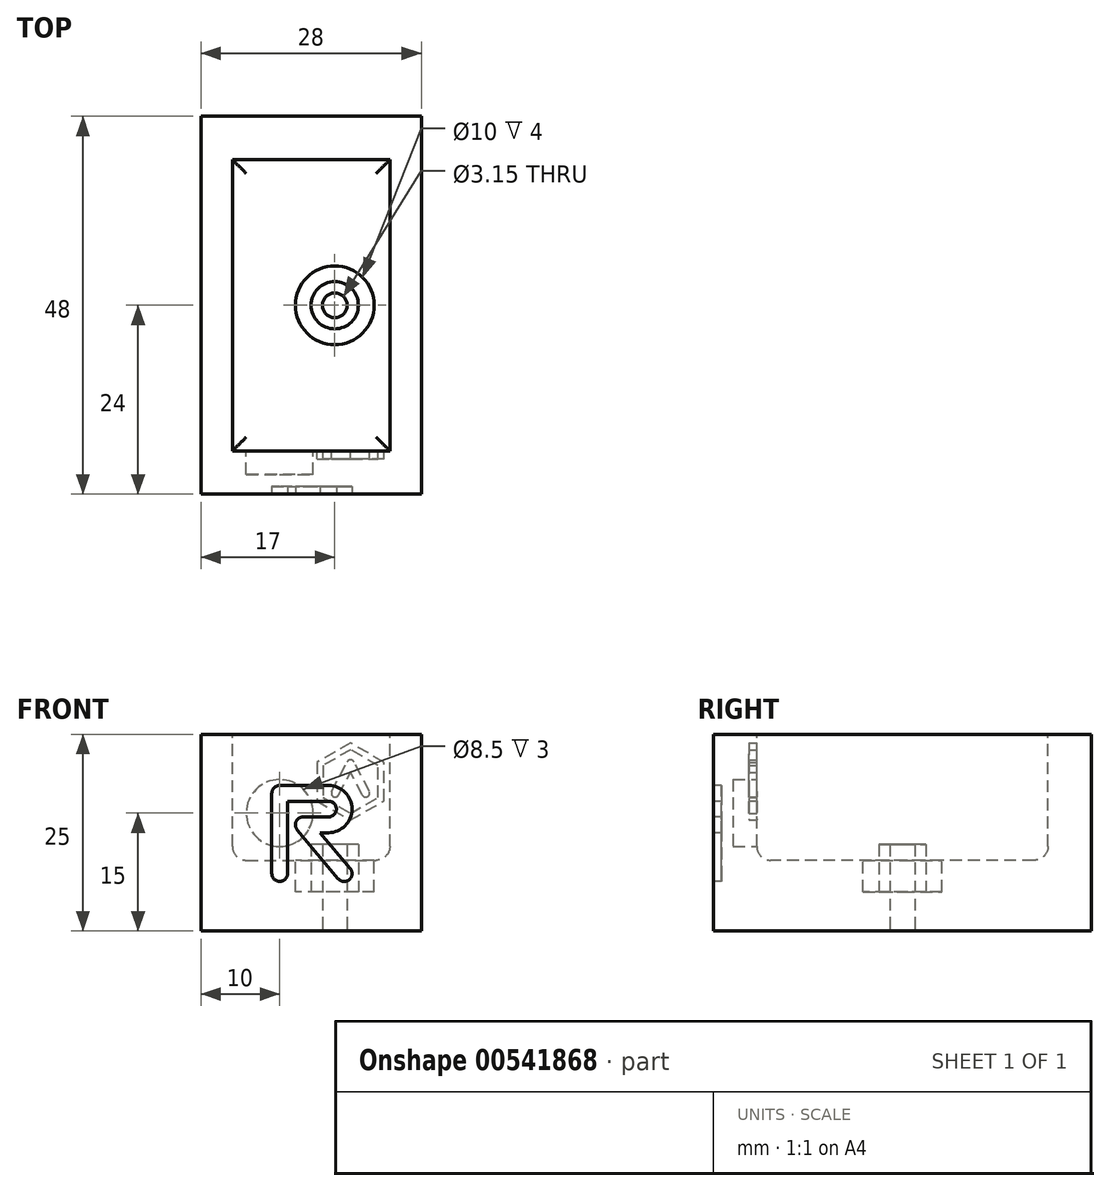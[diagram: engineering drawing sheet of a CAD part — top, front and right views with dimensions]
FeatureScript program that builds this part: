
annotation { "Feature Type Name" : "Feature", "Feature Type Description" : "" }
export const myFeature = defineFeature(function(context is Context, id is Id, definition is map)
    precondition{}
    {
        {
            var Q0;
            Q0=qCreatedBy(makeId("Top.planeOp"),FACE);
            var sketch = newSketch(context, id + "F0", { "sketchPlane" : qUnion([Q0])});
            skLineSegment(sketch, "E0.bottom", {"start": v(-28, 48) * mm, "end": v(0, 48) * mm});
            skLineSegment(sketch, "E0.top", {"start": v(-28, 0) * mm, "end": v(0, 0) * mm});
            skLineSegment(sketch, "E0.left", {"start": v(-28, 48) * mm, "end": v(-28, 0) * mm});
            skLineSegment(sketch, "E0.right", {"start": v(0, 48) * mm, "end": v(0, 0) * mm});
            skSolve(sketch);
        }
        {
            var Q0;
            Q0=makeQuery(id+"F0.imprint","IMPRINT",FACE,{"disambiguationData":[TD([[makeQuery(id+"F0.imprint","IMPRINT",EDGE,{"derivedFrom":sQuery(id+"F0.wireOp",EDGE,"E0.bottom")}),-1.0]])]});
            extrude(context, id + "F1", {"entities" : qUnion([Q0]), "depth" : 25 * mm, "offsetDistance" : 25 * mm});
        }
        {
            var Q0;
            Q0=makeQuery(id+"F1.opExtrude","CAP_FACE",FACE,{"disambiguationData":[OSD([sQuery(id+"F0.wireOp",EDGE,"E0.bottom"),sQuery(id+"F0.wireOp",EDGE,"E0.top"),sQuery(id+"F0.wireOp",EDGE,"E0.left"),sQuery(id+"F0.wireOp",EDGE,"E0.right")])],"isStart":false});
            var sketch = newSketch(context, id + "F2", { "sketchPlane" : qUnion([Q0])});
            skLineSegment(sketch, "E1.bottom", {"start": v(-24, 42.5) * mm, "end": v(-4, 42.5) * mm});
            skLineSegment(sketch, "E1.top", {"start": v(-24, 5.5) * mm, "end": v(-4, 5.5) * mm});
            skLineSegment(sketch, "E1.left", {"start": v(-24, 42.5) * mm, "end": v(-24, 5.5) * mm});
            skLineSegment(sketch, "E1.right", {"start": v(-4, 42.5) * mm, "end": v(-4, 5.5) * mm});
            skSolve(sketch);
        }
        {
            var Q0;
            Q0=qSketchRegion(id+"F2",true);
            extrude(context, id + "F3", {"entities" : qUnion([Q0]), "operationType" : NewBodyOperationType.REMOVE, "oppositeDirection" : true, "depth" : 16 * mm, "offsetDistance" : 25 * mm});
        }
        {
            var Q0;
            Q0=makeQuery(id+"F3.boolean.opBoolean","COPY",FACE,{"derivedFrom":makeQuery(id+"F3.opExtrude","CAP_FACE",FACE,{"disambiguationData":[OSD([sQuery(id+"F2.wireOp",EDGE,"E1.bottom"),sQuery(id+"F2.wireOp",EDGE,"E1.top"),sQuery(id+"F2.wireOp",EDGE,"E1.left"),sQuery(id+"F2.wireOp",EDGE,"E1.right")])],"isStart":false})});
            var sketch = newSketch(context, id + "F4", { "sketchPlane" : qUnion([Q0])});
            skCircle(sketch, "E2", {"center": v(-11, 24) * mm, "radius": 3 * mm});
            skCircle(sketch, "E3", {"center": v(-11, 24) * mm, "radius": 1.57 * mm});
            skSolve(sketch);
        }
        {
            var Q0;
            Q0=qSketchRegion(id+"F4",true);
            extrude(context, id + "F5", {"entities" : qUnion([Q0]), "operationType" : NewBodyOperationType.ADD, "depth" : 2 * mm, "offsetDistance" : 25 * mm});
        }
        {
            var Q0;
            {var subQ0=sQuery(id+"F2.wireOp",EDGE,"E1.right");var subQ1=sQuery(id+"F2.wireOp",EDGE,"E1.left");var subQ2=sQuery(id+"F2.wireOp",EDGE,"E1.top");var subQ3=sQuery(id+"F2.wireOp",EDGE,"E1.bottom");Q0=makeQuery(id+"F5.boolean.opBoolean","SPLIT",FACE,{"disambiguationData":[TD([makeQuery(id+"F3.boolean.opBoolean","COPY",FACE,{"derivedFrom":makeQuery(id+"F3.opExtrude","SWEPT_FACE",FACE,{"disambiguationData":[OSD([subQ3])]})})])],"derivedFrom":makeQuery(id+"F3.boolean.opBoolean","COPY",FACE,{"derivedFrom":makeQuery(id+"F3.opExtrude","CAP_FACE",FACE,{"disambiguationData":[OSD([subQ3,subQ2,subQ1,subQ0])],"isStart":false})})});}
            var sketch = newSketch(context, id + "F6", { "sketchPlane" : qUnion([Q0])});
            skCircle(sketch, "E4", {"center": v(-11, 24) * mm, "radius": 5 * mm});
            skCircle(sketch, "E5", {"center": v(-11, 24) * mm, "radius": 3 * mm});
            skSolve(sketch);
        }
        {
            var Q0;
            Q0=qSketchRegion(id+"F6",true);
            extrude(context, id + "F7", {"entities" : qUnion([Q0]), "operationType" : NewBodyOperationType.REMOVE, "oppositeDirection" : true, "depth" : 4 * mm, "offsetDistance" : 25 * mm});
        }
        {
            var Q0;
            Q0=makeQuery(id+"F3.boolean.opBoolean","COPY",FACE,{"derivedFrom":makeQuery(id+"F3.opExtrude","SWEPT_FACE",FACE,{"disambiguationData":[OSD([sQuery(id+"F2.wireOp",EDGE,"E1.top")])]})});
            var sketch = newSketch(context, id + "F8", { "sketchPlane" : qUnion([Q0])});
            skCircle(sketch, "E6", {"center": v(18, 15) * mm, "radius": 4.25 * mm});
            skSolve(sketch);
        }
        {
            var Q0;
            Q0=makeQuery(id+"F8.imprint","IMPRINT",FACE,{"disambiguationData":[TD([[makeQuery(id+"F8.imprint","IMPRINT",EDGE,{"derivedFrom":sQuery(id+"F8.wireOp",EDGE,"E6")}),1.0]])]});
            var Q1;
            Q1=sQuery(id+"F8.wireOp",EDGE,"E6");
            extrude(context, id + "F9", {"entities" : qUnion([Q0]), "operationType" : NewBodyOperationType.REMOVE, "surfaceEntities" : qUnion([Q1]), "oppositeDirection" : true, "depth" : 3 * mm, "offsetDistance" : 25 * mm});
        }
        {
            var Q0;
            Q0=makeQuery(id+"F5.boolean.opBoolean","SPLIT",FACE,{"disambiguationData":[TD([makeQuery(id+"F5.opExtrude","SWEPT_FACE",FACE,{"disambiguationData":[OSD([sQuery(id+"F4.wireOp",EDGE,"E3")])]})])],"derivedFrom":makeQuery(id+"F3.boolean.opBoolean","COPY",FACE,{"derivedFrom":makeQuery(id+"F3.opExtrude","CAP_FACE",FACE,{"disambiguationData":[OSD([sQuery(id+"F2.wireOp",EDGE,"E1.bottom"),sQuery(id+"F2.wireOp",EDGE,"E1.top"),sQuery(id+"F2.wireOp",EDGE,"E1.left"),sQuery(id+"F2.wireOp",EDGE,"E1.right")])],"isStart":false})})});
            extrude(context, id + "F10", {"entities" : qUnion([Q0]), "operationType" : NewBodyOperationType.REMOVE, "endBound" : BoundingType.THROUGH_ALL, "oppositeDirection" : true, "depth" : 25 * mm, "offsetDistance" : 25 * mm});
        }
        {
            var Q0;
            Q0=makeQuery(id+"F3.boolean.opBoolean","COPY",FACE,{"derivedFrom":makeQuery(id+"F3.opExtrude","SWEPT_FACE",FACE,{"disambiguationData":[OSD([sQuery(id+"F2.wireOp",EDGE,"E1.bottom")])]})});
            var sketch = newSketch(context, id + "F11", { "sketchPlane" : qUnion([Q0])});
            skCircle(sketch, "E7", {"center": v(-18, 15) * mm, "radius": 4.25 * mm});
            skSolve(sketch);
        }
        {
            var Q0;
            Q0=makeQuery(id+"F1.opExtrude","SWEPT_FACE",FACE,{"disambiguationData":[OSD([sQuery(id+"F0.wireOp",EDGE,"E0.bottom")])]});
            var sketch = newSketch(context, id + "F12", { "sketchPlane" : qUnion([Q0])});
            skLineSegment(sketch, "E8", {"start": v(10, 19) * mm, "end": v(10, 7) * mm});
            skLineSegment(sketch, "E9", {"start": v(11, 6) * mm, "end": v(17, 6) * mm});
            skLineSegment(sketch, "E10", {"start": v(18, 7) * mm, "end": v(18, 7) * mm});
            skLineSegment(sketch, "E11", {"start": v(17, 8) * mm, "end": v(12.5, 8) * mm});
            skLineSegment(sketch, "E12", {"start": v(12, 8.5) * mm, "end": v(12, 19) * mm});
            skLineSegment(sketch, "E13", {"start": v(11, 20) * mm, "end": v(11, 20) * mm});
            skPoint(sketch, "E14.visualSharp", {"position": v(10, 20) * mm});
            skArc(sketch, "E14.filletArc", {"start": v(11, 20) * mm, "mid": v(10.3, 19.7) * mm, "end": v(10, 19) * mm});
            skPoint(sketch, "E15.visualSharp", {"position": v(12, 20) * mm});
            skArc(sketch, "E15.filletArc", {"start": v(12, 19) * mm, "mid": v(11.7, 19.7) * mm, "end": v(11, 20) * mm});
            skPoint(sketch, "E16.visualSharp", {"position": v(10, 6) * mm});
            skArc(sketch, "E16.filletArc", {"start": v(10, 7) * mm, "mid": v(10.3, 6.3) * mm, "end": v(11, 6) * mm});
            skPoint(sketch, "E17.visualSharp", {"position": v(12, 8) * mm});
            skArc(sketch, "E17.filletArc", {"start": v(12, 8.5) * mm, "mid": v(12.15, 8.15) * mm, "end": v(12.5, 8) * mm});
            skPoint(sketch, "E18.visualSharp", {"position": v(18, 8) * mm});
            skArc(sketch, "E18.filletArc", {"start": v(18, 7) * mm, "mid": v(17.7, 7.7) * mm, "end": v(17, 8) * mm});
            skPoint(sketch, "E19.visualSharp", {"position": v(18, 6) * mm});
            skArc(sketch, "E19.filletArc", {"start": v(17, 6) * mm, "mid": v(17.7, 6.3) * mm, "end": v(18, 7) * mm});
            skSolve(sketch);
        }
        {
            var Q0;
            Q0=makeQuery(id+"F1.opExtrude","SWEPT_FACE",FACE,{"disambiguationData":[OSD([sQuery(id+"F0.wireOp",EDGE,"E0.top")])]});
            var sketch = newSketch(context, id + "F13", { "sketchPlane" : qUnion([Q0])});
            skLineSegment(sketch, "E20", {"start": v(-17, 7.3) * mm, "end": v(-17, 18.5) * mm});
            skLineSegment(sketch, "E21", {"start": v(-17, 18.5) * mm, "end": v(-11.8, 18.5) * mm});
            skLineSegment(sketch, "E22", {"start": v(-17, 16.5) * mm, "end": v(-11.8, 16.5) * mm});
            skLineSegment(sketch, "E23", {"start": v(-17, 18.5) * mm, "end": v(-18, 18.5) * mm});
            skLineSegment(sketch, "E24", {"start": v(-19, 17.5) * mm, "end": v(-19, 7.3) * mm});
            skLineSegment(sketch, "E25", {"start": v(-15, 14.5) * mm, "end": v(-11.8, 14.5) * mm});
            skArc(sketch, "E26", {"start": v(-11.8, 16.5) * mm, "mid": v(-10.8, 15.5) * mm, "end": v(-11.8, 14.5) * mm});
            skLineSegment(sketch, "E27", {"start": v(-15, 12.5) * mm, "end": v(-11.8, 12.5) * mm});
            skArc(sketch, "E28", {"start": v(-11.8, 18.5) * mm, "mid": v(-8.8, 15.5) * mm, "end": v(-11.8, 12.5) * mm});
            skArc(sketch, "E29", {"start": v(-19, 7.3) * mm, "mid": v(-18, 6.3) * mm, "end": v(-17, 7.3) * mm});
            skPoint(sketch, "E30.visualSharp", {"position": v(-19, 18.5) * mm});
            skArc(sketch, "E30.filletArc", {"start": v(-18, 18.5) * mm, "mid": v(-18.7, 18.2) * mm, "end": v(-19, 17.5) * mm});
            skCircle(sketch, "E31", {"center": v(-15, 13.5) * mm, "radius": 1 * mm});
            skLineSegment(sketch, "E32", {"start": v(-10.56, 6.66) * mm, "end": v(-9.03, 7.94) * mm, "construction": true});
            skLineSegment(sketch, "E33", {"start": v(-10.56, 6.66) * mm, "end": v(-15.77, 12.86) * mm});
            skLineSegment(sketch, "E34", {"start": v(-9.03, 7.94) * mm, "end": v(-14.23, 14.14) * mm});
            skArc(sketch, "E35", {"start": v(-10.56, 6.66) * mm, "mid": v(-9.16, 6.53) * mm, "end": v(-9.03, 7.94) * mm});
            skLineSegment(sketch, "E36", {"start": v(-8.8, 15.5) * mm, "end": v(-8.8, 7.3) * mm, "construction": true});
            skLineSegment(sketch, "E37", {"start": v(-8.8, 7.3) * mm, "end": v(-19, 7.3) * mm, "construction": true});
            skSolve(sketch);
        }
        {
            var Q0;
            Q0=qSketchRegion(id+"F13",true);
            extrude(context, id + "F14", {"entities" : qUnion([Q0]), "operationType" : NewBodyOperationType.REMOVE, "oppositeDirection" : true, "depth" : 1 * mm, "offsetDistance" : 25 * mm});
        }
        {
            var Q0;
            Q0=makeQuery(id+"F3.boolean.opBoolean","COPY",FACE,{"derivedFrom":makeQuery(id+"F3.opExtrude","SWEPT_FACE",FACE,{"disambiguationData":[OSD([sQuery(id+"F2.wireOp",EDGE,"E1.bottom")])]})});
            var sketch = newSketch(context, id + "F15", { "sketchPlane" : qUnion([Q0])});
            skCircle(sketch, "E38.cCircle", {"center": v(-9, 19) * mm, "radius": 4.25 * mm, "construction": true});
            skLineSegment(sketch, "E38.0", {"start": v(-4.75, 16.55) * mm, "end": v(-9, 14.1) * mm});
            skLineSegment(sketch, "E38.1", {"start": v(-9, 14.1) * mm, "end": v(-13.25, 16.55) * mm});
            skLineSegment(sketch, "E38.2", {"start": v(-13.25, 16.55) * mm, "end": v(-13.25, 21.45) * mm});
            skLineSegment(sketch, "E38.3", {"start": v(-13.25, 21.45) * mm, "end": v(-9, 23.9) * mm});
            skLineSegment(sketch, "E38.4", {"start": v(-9, 23.9) * mm, "end": v(-4.75, 21.45) * mm});
            skLineSegment(sketch, "E38.5", {"start": v(-4.75, 21.45) * mm, "end": v(-4.75, 16.55) * mm});
            skPoint(sketch, "E38.0.midPoint", {"position": v(-6.87, 15.32) * mm});
            skCircle(sketch, "E39.cCircle", {"center": v(-9, 19) * mm, "radius": 3.5 * mm, "construction": true});
            skLineSegment(sketch, "E39.0", {"start": v(-12.5, 16.98) * mm, "end": v(-12.5, 21.02) * mm});
            skLineSegment(sketch, "E39.1", {"start": v(-12.5, 21.02) * mm, "end": v(-9, 23.04) * mm});
            skLineSegment(sketch, "E39.2", {"start": v(-9, 23.04) * mm, "end": v(-5.5, 21.02) * mm});
            skLineSegment(sketch, "E39.3", {"start": v(-5.5, 21.02) * mm, "end": v(-5.5, 16.98) * mm});
            skLineSegment(sketch, "E39.4", {"start": v(-5.5, 16.98) * mm, "end": v(-9, 14.96) * mm});
            skLineSegment(sketch, "E39.5", {"start": v(-9, 14.96) * mm, "end": v(-12.5, 16.98) * mm});
            skPoint(sketch, "E39.0.midPoint", {"position": v(-12.5, 19) * mm});
            skCircle(sketch, "E40", {"center": v(-9, 21.25) * mm, "radius": 0.5 * mm});
            skLineSegment(sketch, "E41", {"start": v(-11.38, 17.75) * mm, "end": v(-9.44, 21.48) * mm});
            skLineSegment(sketch, "E42", {"start": v(-6.62, 17.75) * mm, "end": v(-8.56, 21.48) * mm});
            skLineSegment(sketch, "E43", {"start": v(-11.38, 17.75) * mm, "end": v(-10.5, 17.3) * mm});
            skLineSegment(sketch, "E44", {"start": v(-7.5, 17.3) * mm, "end": v(-6.62, 17.75) * mm});
            skLineSegment(sketch, "E45", {"start": v(-10.5, 17.3) * mm, "end": v(-8.56, 21.02) * mm});
            skLineSegment(sketch, "E46", {"start": v(-7.5, 17.3) * mm, "end": v(-9.44, 21.02) * mm});
            skArc(sketch, "E47", {"start": v(-11.38, 17.75) * mm, "mid": v(-11.17, 17.08) * mm, "end": v(-10.5, 17.3) * mm});
            skArc(sketch, "E48", {"start": v(-6.62, 17.75) * mm, "mid": v(-6.83, 17.08) * mm, "end": v(-7.5, 17.3) * mm});
            skSolve(sketch);
        }
        {
            var Q0;
            Q0=makeQuery(id+"F3.boolean.opBoolean","COPY",FACE,{"derivedFrom":makeQuery(id+"F3.opExtrude","SWEPT_FACE",FACE,{"disambiguationData":[OSD([sQuery(id+"F2.wireOp",EDGE,"E1.top")])]})});
            var sketch = newSketch(context, id + "F16", { "sketchPlane" : qUnion([Q0])});
            skCircle(sketch, "E49.cCircle", {"center": v(9, 19) * mm, "radius": 4.25 * mm, "construction": true});
            skLineSegment(sketch, "E49.0", {"start": v(13.25, 16.55) * mm, "end": v(9, 14.1) * mm});
            skLineSegment(sketch, "E49.1", {"start": v(9, 14.1) * mm, "end": v(4.75, 16.55) * mm});
            skLineSegment(sketch, "E49.2", {"start": v(4.75, 16.55) * mm, "end": v(4.75, 21.45) * mm});
            skLineSegment(sketch, "E49.3", {"start": v(4.75, 21.45) * mm, "end": v(9, 23.9) * mm});
            skLineSegment(sketch, "E49.4", {"start": v(9, 23.9) * mm, "end": v(13.25, 21.45) * mm});
            skLineSegment(sketch, "E49.5", {"start": v(13.25, 21.45) * mm, "end": v(13.25, 16.55) * mm});
            skPoint(sketch, "E49.0.midPoint", {"position": v(11.12, 15.32) * mm});
            skCircle(sketch, "E50.cCircle", {"center": v(9, 19) * mm, "radius": 3.5 * mm, "construction": true});
            skLineSegment(sketch, "E50.0", {"start": v(5.5, 16.98) * mm, "end": v(5.5, 21.02) * mm});
            skLineSegment(sketch, "E50.1", {"start": v(5.5, 21.02) * mm, "end": v(9, 23.04) * mm});
            skLineSegment(sketch, "E50.2", {"start": v(9, 23.04) * mm, "end": v(12.5, 21.02) * mm});
            skLineSegment(sketch, "E50.3", {"start": v(12.5, 21.02) * mm, "end": v(12.5, 16.98) * mm});
            skLineSegment(sketch, "E50.4", {"start": v(12.5, 16.98) * mm, "end": v(9, 14.96) * mm});
            skLineSegment(sketch, "E50.5", {"start": v(9, 14.96) * mm, "end": v(5.5, 16.98) * mm});
            skPoint(sketch, "E50.0.midPoint", {"position": v(5.5, 19) * mm});
            skCircle(sketch, "E51", {"center": v(9, 21.25) * mm, "radius": 0.5 * mm});
            skLineSegment(sketch, "E52", {"start": v(6.62, 17.75) * mm, "end": v(8.56, 21.48) * mm});
            skLineSegment(sketch, "E53", {"start": v(11.38, 17.75) * mm, "end": v(9.44, 21.48) * mm});
            skLineSegment(sketch, "E54", {"start": v(6.62, 17.75) * mm, "end": v(7.5, 17.3) * mm});
            skLineSegment(sketch, "E55", {"start": v(10.5, 17.3) * mm, "end": v(11.38, 17.75) * mm});
            skLineSegment(sketch, "E56", {"start": v(7.5, 17.3) * mm, "end": v(9.44, 21.02) * mm});
            skLineSegment(sketch, "E57", {"start": v(10.5, 17.3) * mm, "end": v(8.56, 21.02) * mm});
            skArc(sketch, "E58", {"start": v(6.62, 17.75) * mm, "mid": v(6.83, 17.08) * mm, "end": v(7.5, 17.3) * mm});
            skArc(sketch, "E59", {"start": v(11.38, 17.75) * mm, "mid": v(11.17, 17.08) * mm, "end": v(10.5, 17.3) * mm});
            skSolve(sketch);
        }
        {
            var Q0;
            Q0=qSketchRegion(id+"F16",true);
            var Q1;
            Q1=makeQuery(id+"F16.imprint","IMPRINT",FACE,{"disambiguationData":[TD([[makeQuery(id+"F16.imprint","IMPRINT",EDGE,{"derivedFrom":sQuery(id+"F16.wireOp",EDGE,"E54")}),-1.0]])]});
            var Q2;
            {var subQ4=sQuery(id+"F16.wireOp",EDGE,"E52");Q2=makeQuery(id+"F16.imprint","IMPRINT",FACE,{"disambiguationData":[TD([[makeQuery(id+"F16.imprint","IMPRINT",EDGE,{"derivedFrom":subQ4}),-1.0]])]});}
            var Q3;
            {var subQ0=sQuery(id+"F16.wireOp",EDGE,"E56");var subQ1=sQuery(id+"F16.wireOp",EDGE,"E51");var subQ2=makeQuery(id+"F16.imprint","INTERSECT",VERTEX,{"derivedFrom":[subQ1,subQ0]});Q3=makeQuery(id+"F16.imprint","IMPRINT",FACE,{"disambiguationData":[TD([[makeQuery(id+"F16.imprint","IMPRINT",EDGE,{"disambiguationData":[TD([[subQ2,1.0]])],"derivedFrom":subQ1}),-1.0]])]});}
            var Q4;
            {var subQ0=sQuery(id+"F16.wireOp",EDGE,"E51");var subQ1=makeQuery(id+"F16.imprint","INTERSECT",VERTEX,{"derivedFrom":[subQ0,sQuery(id+"F16.wireOp",EDGE,"E52")]});Q4=makeQuery(id+"F16.imprint","IMPRINT",FACE,{"disambiguationData":[TD([[makeQuery(id+"F16.imprint","IMPRINT",EDGE,{"disambiguationData":[TD([[subQ1,1.0]])],"derivedFrom":subQ0}),1.0]])]});}
            var Q5;
            {var subQ6=sQuery(id+"F16.wireOp",EDGE,"E53");Q5=makeQuery(id+"F16.imprint","IMPRINT",FACE,{"disambiguationData":[TD([[makeQuery(id+"F16.imprint","IMPRINT",EDGE,{"derivedFrom":subQ6}),1.0]])]});}
            var Q6;
            Q6=makeQuery(id+"F16.imprint","IMPRINT",FACE,{"disambiguationData":[TD([[makeQuery(id+"F16.imprint","IMPRINT",EDGE,{"derivedFrom":sQuery(id+"F16.wireOp",EDGE,"E55")}),-1.0]])]});
            extrude(context, id + "F17", {"entities" : qUnion([Q0, Q1, Q2, Q3, Q4, Q5, Q6]), "operationType" : NewBodyOperationType.REMOVE, "oppositeDirection" : true, "depth" : 1 * mm, "offsetDistance" : 25 * mm});
        }
        {
            var Q0;
            Q0=makeQuery(id+"F3.boolean.opBoolean","COPY",EDGE,{"derivedFrom":makeQuery(id+"F3.opExtrude","CAP_EDGE",EDGE,{"disambiguationData":[OSD([sQuery(id+"F2.wireOp",EDGE,"E1.left")])],"isStart":false})});
            var Q1;
            Q1=makeQuery(id+"F3.boolean.opBoolean","COPY",EDGE,{"derivedFrom":makeQuery(id+"F3.opExtrude","CAP_EDGE",EDGE,{"disambiguationData":[OSD([sQuery(id+"F2.wireOp",EDGE,"E1.bottom")])],"isStart":false})});
            var Q2;
            Q2=makeQuery(id+"F3.boolean.opBoolean","COPY",EDGE,{"derivedFrom":makeQuery(id+"F3.opExtrude","CAP_EDGE",EDGE,{"disambiguationData":[OSD([sQuery(id+"F2.wireOp",EDGE,"E1.right")])],"isStart":false})});
            var Q3;
            Q3=makeQuery(id+"F3.boolean.opBoolean","COPY",EDGE,{"derivedFrom":makeQuery(id+"F3.opExtrude","CAP_EDGE",EDGE,{"disambiguationData":[OSD([sQuery(id+"F2.wireOp",EDGE,"E1.top")])],"isStart":false})});
            fillet(context, id + "F18", {"entities" : qUnion([Q0, Q1, Q2, Q3]), "radius" : 1.75 * mm, "tangentPropagation" : true, "allowEdgeOverflow" : false});
        }
    });
